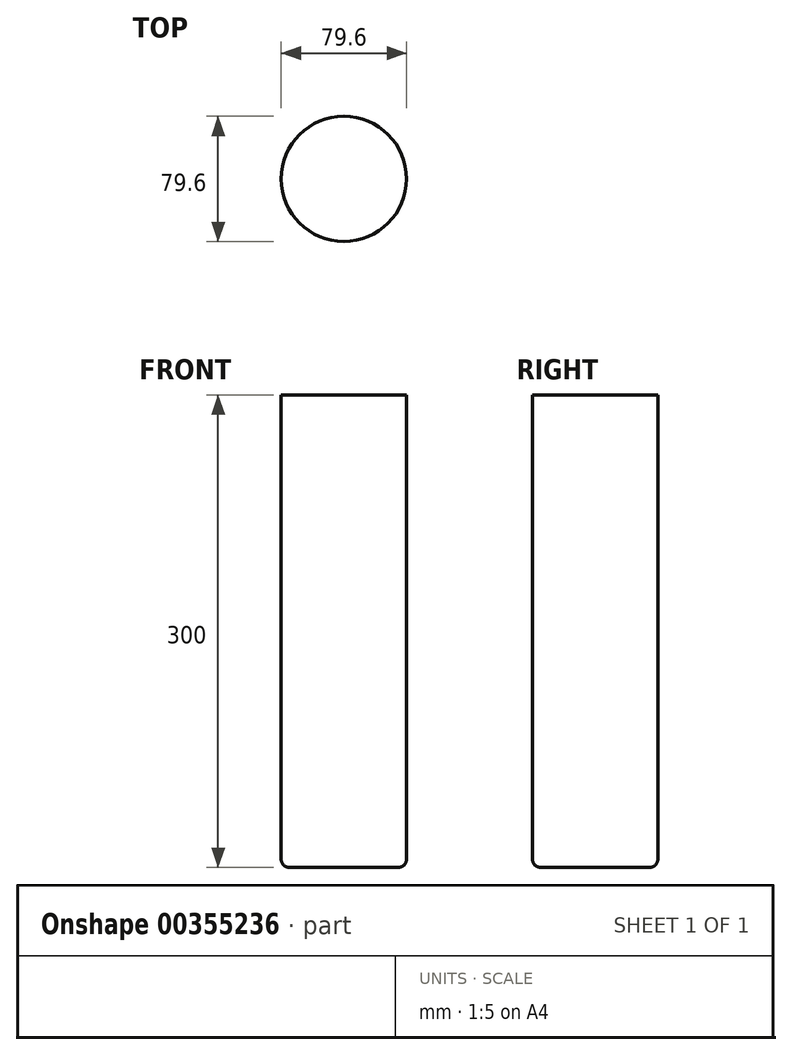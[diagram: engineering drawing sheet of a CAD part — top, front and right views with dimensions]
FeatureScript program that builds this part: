
annotation { "Feature Type Name" : "Feature", "Feature Type Description" : "" }
export const myFeature = defineFeature(function(context is Context, id is Id, definition is map)
    precondition{}
    {
        {
            var Q0;
            Q0=qCreatedBy(makeId("Top.planeOp"),FACE);
            var sketch = newSketch(context, id + "F0", { "sketchPlane" : qUnion([Q0])});
            skCircle(sketch, "E0", {"center": v(0, 0) * mm, "radius": 39.8 * mm});
            skSolve(sketch);
        }
        {
            var Q0;
            Q0=makeQuery(id+"F0.imprint","IMPRINT",FACE,{"disambiguationData":[TD([[makeQuery(id+"F0.imprint","IMPRINT",EDGE,{"derivedFrom":sQuery(id+"F0.wireOp",EDGE,"E0")}),1.0]])]});
            extrude(context, id + "F1", {"entities" : qUnion([Q0]), "depth" : 300 * mm});
        }
        {
            var Q0;
            Q0=makeQuery(id+"F1.opExtrude","CAP_EDGE",EDGE,{"disambiguationData":[OSD([sQuery(id+"F0.wireOp",EDGE,"E0")])],"isStart":true});
            fillet(context, id + "F2", {"entities" : qUnion([Q0]), "radius" : 5.08 * mm, "tangentPropagation" : true, "allowEdgeOverflow" : false});
        }
    });
